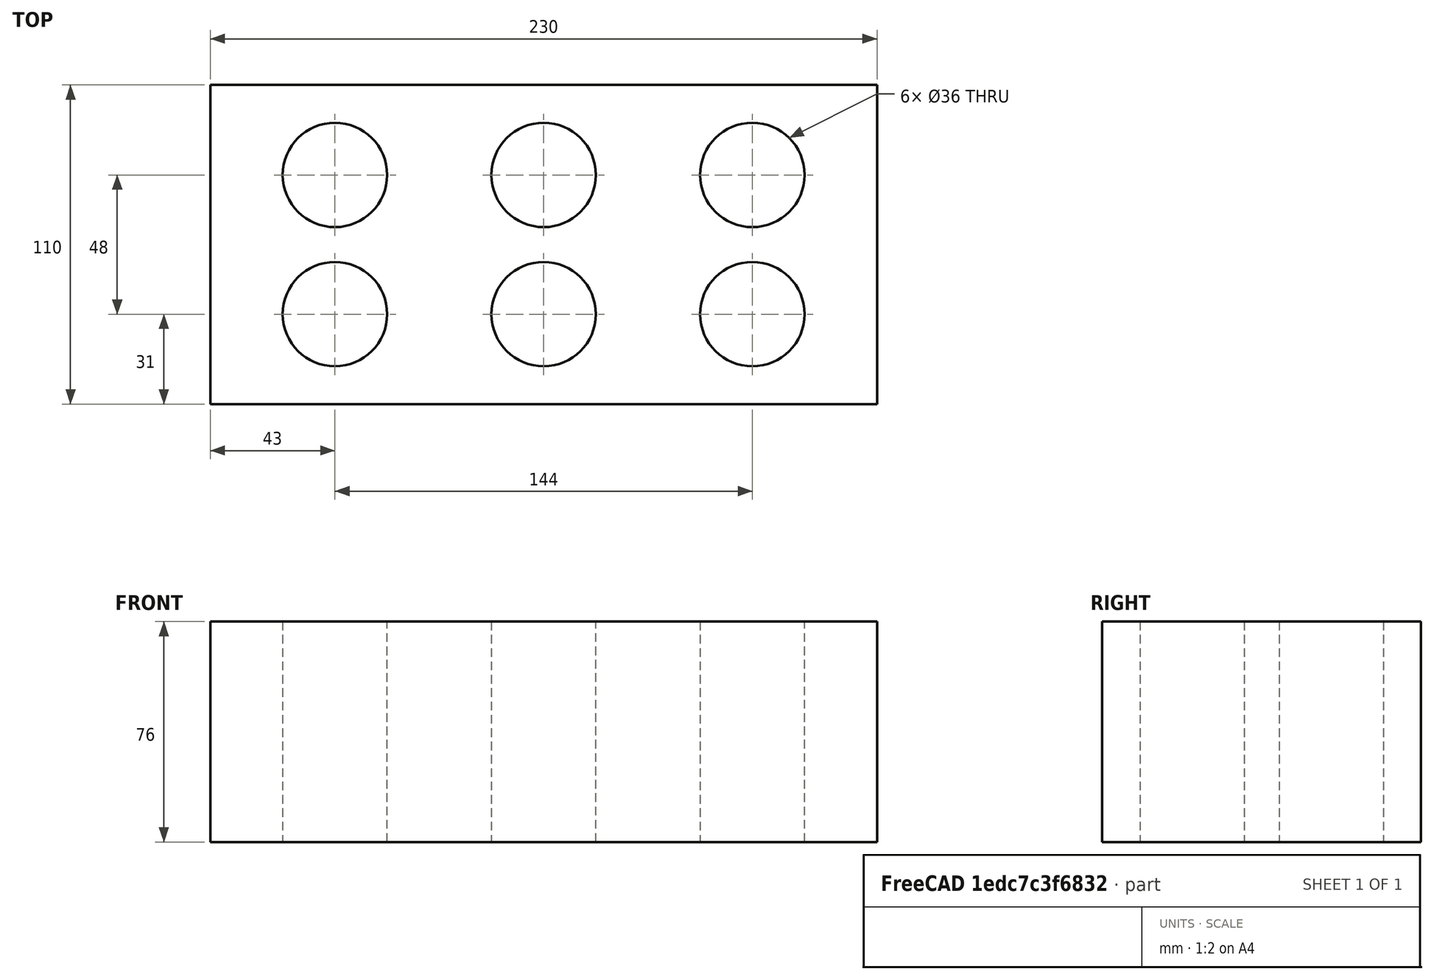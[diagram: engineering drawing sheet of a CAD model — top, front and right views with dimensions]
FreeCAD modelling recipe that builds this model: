
FCSTD DOCUMENT  (FreeCAD 0.21R33694 (Git))
Label: OJT1_T09_R03_Tocho
License: All rights reserved
LicenseURL: https://en.wikipedia.org/wiki/All_rights_reserved
objects: Part::Cylinder×6, Part::Box×1, Part::MultiFuse×1, Part::Cut×1
note: 9 computed .brp shape members not serialized (recipe doc carries the construction recipe); baked Part::Feature solids carry a one-line shape summary decoded from their .brp

FEATURE [Part::Box] Box  label="Cub-Base"
  AttacherType = Attacher::AttachEngine3D
  Height = 76
  Length = 230
  Placement = pos=(-43,-31,0) rot=(0,0,1;0rad)
  Width = 110
  expr: .Placement.Base.x = -43
  expr: .Placement.Base.y = -31
FEATURE [Part::Cylinder] Cylinder  label="Cilindre1-fila1"
  Angle = 360
  AttacherType = Attacher::AttachEngine3D
  FirstAngle = 0
  Height = 76
  Radius = 18
  SecondAngle = 0
FEATURE [Part::Cylinder] Cylinder001  label="Cilindre2-Fila1"
  Angle = 360
  AttacherType = Attacher::AttachEngine3D
  FirstAngle = 0
  Height = 76
  Placement = pos=(72,0,0) rot=(0,0,1;0rad)
  Radius = 18
  SecondAngle = 0
  expr: .Placement.Base.x = 72
FEATURE [Part::Cylinder] Cylinder002  label="Cilindre3_Fila1"
  Angle = 360
  AttacherType = Attacher::AttachEngine3D
  FirstAngle = 0
  Height = 76
  Placement = pos=(144,0,0) rot=(0,0,1;0rad)
  Radius = 18
  SecondAngle = 0
  expr: .Placement.Base.x = 144
FEATURE [Part::Cylinder] Cylinder003  label="Cilindre2-Fila2"
  Angle = 360
  AttacherType = Attacher::AttachEngine3D
  FirstAngle = 0
  Height = 76
  Placement = pos=(72,48,0) rot=(0,0,1;0rad)
  Radius = 18
  SecondAngle = 0
  expr: .Placement.Base.x = 72
  expr: .Placement.Base.y = 48
FEATURE [Part::Cylinder] Cylinder004  label="Cilindre1-Fila2"
  Angle = 360
  AttacherType = Attacher::AttachEngine3D
  FirstAngle = 0
  Height = 76
  Placement = pos=(0,48,0) rot=(0,0,1;0rad)
  Radius = 18
  SecondAngle = 0
  expr: .Placement.Base.x = 0
  expr: .Placement.Base.y = 48
FEATURE [Part::Cylinder] Cylinder005  label="Cilindre3-Fila2"
  Angle = 360
  AttacherType = Attacher::AttachEngine3D
  FirstAngle = 0
  Height = 76
  Placement = pos=(144,48,0) rot=(0,0,1;0rad)
  Radius = 18
  SecondAngle = 0
  expr: .Placement.Base.x = 144
  expr: .Placement.Base.y = 48
FEATURE [Part::MultiFuse] Fusion
  Shapes = -> [Cylinder,Cylinder002,Cylinder001,Cylinder003,Cylinder005,Cylinder004]
FEATURE [Part::Cut] Cut
  Base = -> Box
  Tool = -> Fusion
